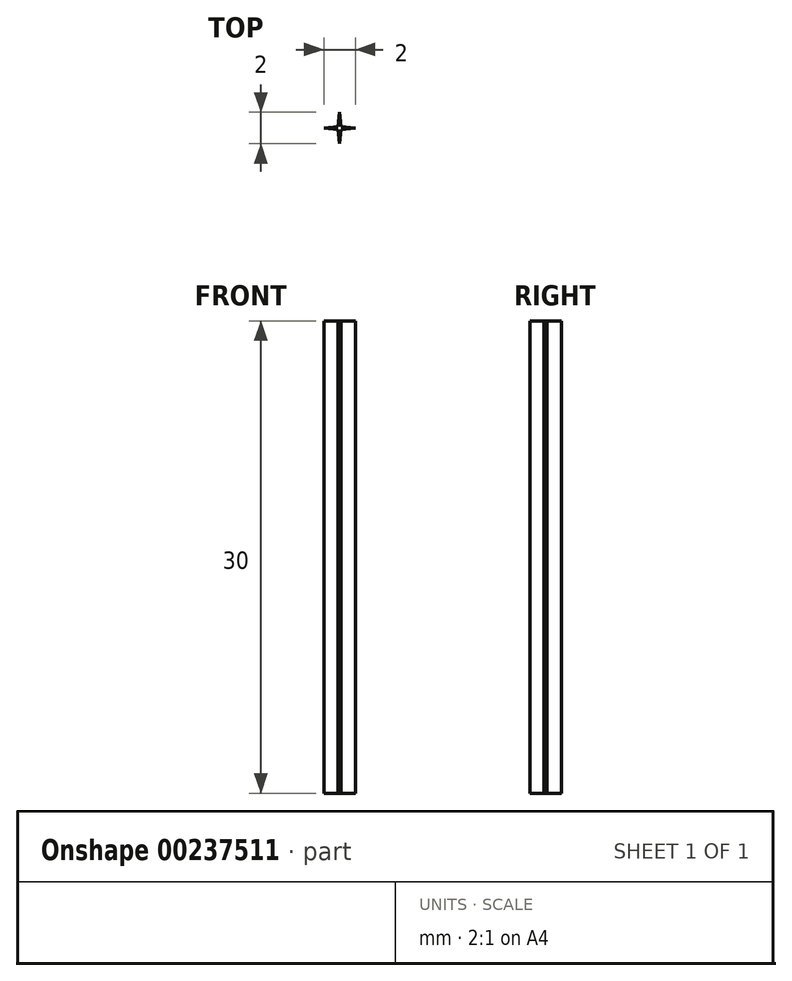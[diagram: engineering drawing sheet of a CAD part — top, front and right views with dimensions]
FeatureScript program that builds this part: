
annotation { "Feature Type Name" : "Feature", "Feature Type Description" : "" }
export const myFeature = defineFeature(function(context is Context, id is Id, definition is map)
    precondition{}
    {
        {
            var Q0;
            Q0=qCreatedBy(makeId("Top.planeOp"),FACE);
            var sketch = newSketch(context, id + "F0", { "sketchPlane" : qUnion([Q0])});
            skPoint(sketch, "E0.middle", {"position": v(0, 0) * mm});
            skPoint(sketch, "E1.orphan", {"position": v(-1, 1) * mm});
            skPoint(sketch, "E2.bottom.start.orphan", {"position": v(-1, -1) * mm});
            skPoint(sketch, "E3.orphan", {"position": v(1, -1) * mm});
            skPoint(sketch, "E4.orphan", {"position": v(1, 1) * mm});
            skPoint(sketch, "E5.endSnap0", {"position": v(-1, 0) * mm});
            skLineSegment(sketch, "E6", {"start": v(-1, 0) * mm, "end": v(-0.1, 0.1) * mm});
            skLineSegment(sketch, "E7", {"start": v(-0.1, -0.1) * mm, "end": v(-1, 0) * mm});
            skLineSegment(sketch, "E8", {"start": v(-0.1, -0.1) * mm, "end": v(0, -1) * mm});
            skLineSegment(sketch, "E9", {"start": v(0.1, -0.1) * mm, "end": v(0, -1) * mm});
            skLineSegment(sketch, "E10", {"start": v(0.1, -0.1) * mm, "end": v(1, 0) * mm});
            skLineSegment(sketch, "E11", {"start": v(1, 0) * mm, "end": v(0.1, 0.1) * mm});
            skLineSegment(sketch, "E12", {"start": v(0.1, 0.1) * mm, "end": v(0, 1) * mm});
            skLineSegment(sketch, "E13", {"start": v(0, 1) * mm, "end": v(-0.1, 0.1) * mm});
            skPoint(sketch, "E14.orphan", {"position": v(-0.1, 1) * mm});
            skPoint(sketch, "E15.right.start.orphan", {"position": v(0.1, 1) * mm});
            skPoint(sketch, "E16.orphan", {"position": v(1, -0.1) * mm});
            skPoint(sketch, "E0.left.end.orphan", {"position": v(1, 0.1) * mm});
            skPoint(sketch, "E17.orphan", {"position": v(0.1, -1) * mm});
            skPoint(sketch, "E2.right.start.orphan", {"position": v(-0.1, -1) * mm});
            skPoint(sketch, "E18.orphan", {"position": v(-1, -0.1) * mm});
            skPoint(sketch, "E19.top.start.orphan", {"position": v(-1, 0.1) * mm});
            skSolve(sketch);
        }
        {
            var Q0;
            Q0=makeQuery(id+"F0.imprint","IMPRINT",FACE,{"disambiguationData":[TD([[makeQuery(id+"F0.imprint","IMPRINT",EDGE,{"derivedFrom":sQuery(id+"F0.wireOp",EDGE,"E6")}),-1.0]])]});
            extrude(context, id + "F1", {"entities" : qUnion([Q0]), "depth" : 30 * mm});
        }
    });
